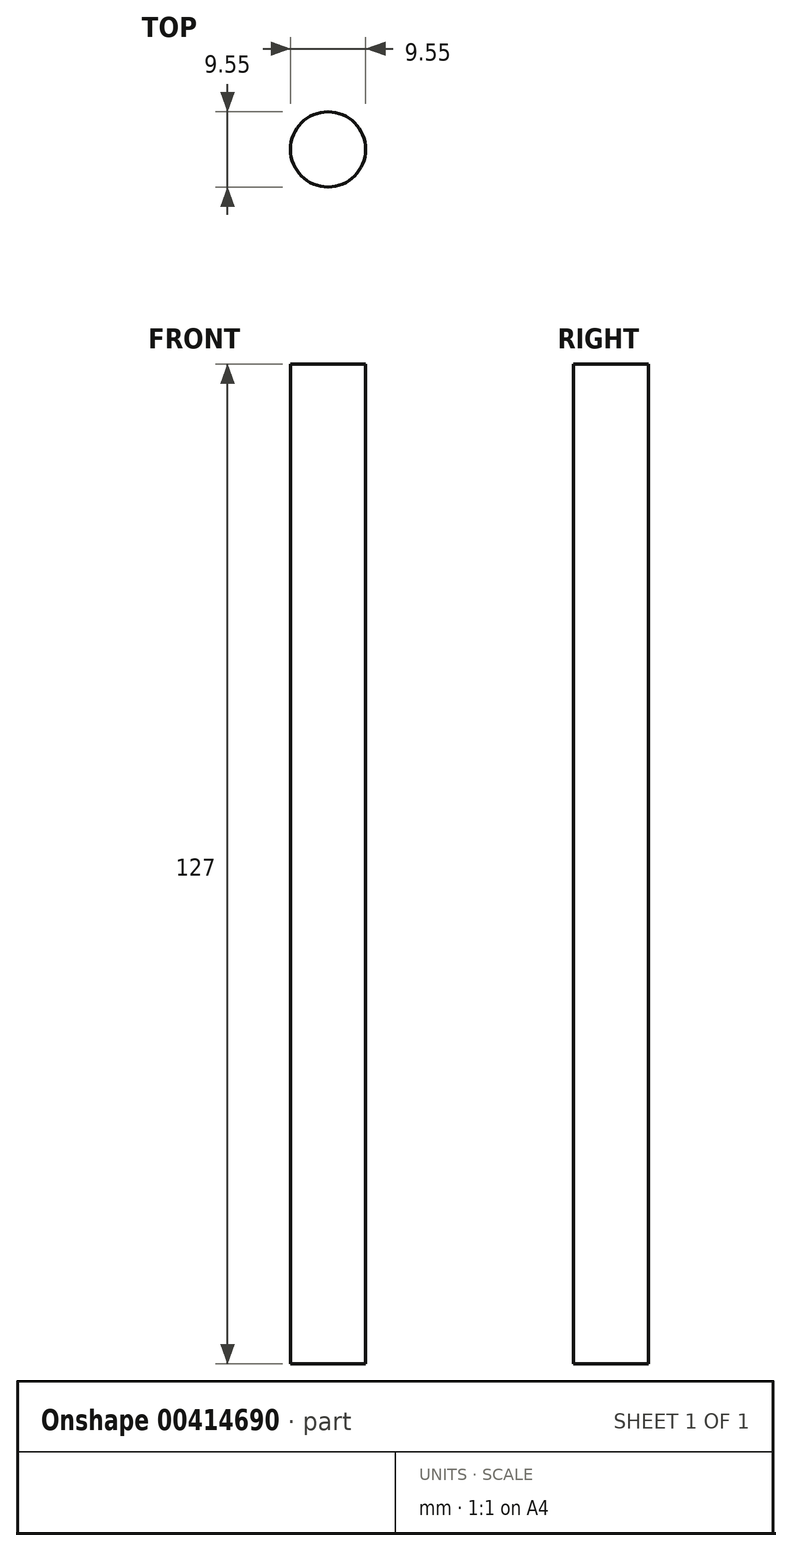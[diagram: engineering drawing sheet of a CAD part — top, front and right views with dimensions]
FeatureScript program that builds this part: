
annotation { "Feature Type Name" : "Feature", "Feature Type Description" : "" }
export const myFeature = defineFeature(function(context is Context, id is Id, definition is map)
    precondition{}
    {
        {
            var Q0;
            Q0=qCreatedBy(makeId("Top.planeOp"),FACE);
            var sketch = newSketch(context, id + "F0", { "sketchPlane" : qUnion([Q0])});
            skLineSegment(sketch, "E0", {"start": v(5.57, 3.82) * mm, "end": v(5.57, 29.22) * mm});
            skLineSegment(sketch, "E1", {"start": v(5.57, 29.22) * mm, "end": v(56.63, 29.22) * mm});
            skLineSegment(sketch, "E2", {"start": v(56.63, 29.22) * mm, "end": v(56.63, 3.82) * mm});
            skLineSegment(sketch, "E3", {"start": v(56.63, 3.82) * mm, "end": v(5.57, 3.82) * mm});
            skCircle(sketch, "E4", {"center": v(26.38, 18.82) * mm, "radius": 4.84 * mm});
            skCircle(sketch, "E5", {"center": v(45.01, 19.3) * mm, "radius": 4.77 * mm});
            skCircle(sketch, "E6", {"center": v(34.85, 11.08) * mm, "radius": 3.49 * mm});
            skSolve(sketch);
        }
        {
            var Q0;
            Q0=sQuery(id+"F0.wireOp",EDGE,"E5");
            extrude(context, id + "F1", {"bodyType" : ToolBodyType.SURFACE, "surfaceEntities" : qUnion([Q0]), "depth" : 127 * mm, "offsetDistance" : 25.4 * mm});
        }
    });
